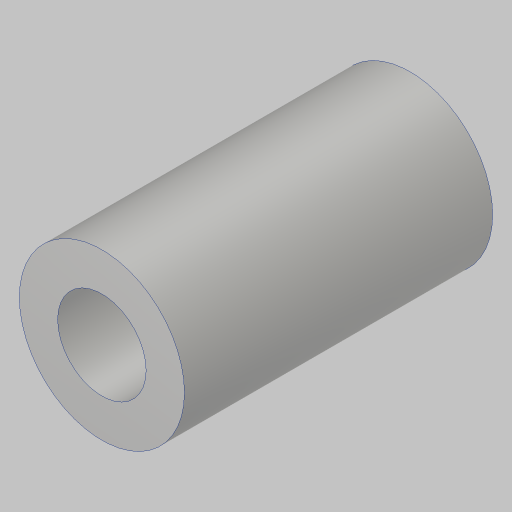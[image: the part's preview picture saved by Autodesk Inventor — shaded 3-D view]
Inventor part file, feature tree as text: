
AUTODESK INVENTOR PART (.ipt)
format: ipt  version: 2023.5 (Build 275446000, 446)  size: 120,832 bytes
history: native  units: in
note: dims shown in document units (in); Inventor stores cm internally (conversion verified against a paired STEP export)
features: extrude x1, hole x1
ambient origin geometry x8: Origin, YZ Plane, XZ Plane, XY Plane, X Axis, Y Axis, Z Axis, Center Point
bodies: Solid1 (feature_tree)
feature tree (2):
  extrude  "Extrusion1"  Depth=0.7in
  hole  "Hole1"  [1 undecoded]
note: 1 required parameter value undecoded (feature->parameter linkage not recoverable at this tier; creation-order binding heuristic only, values carry confidence <= 0.55)
